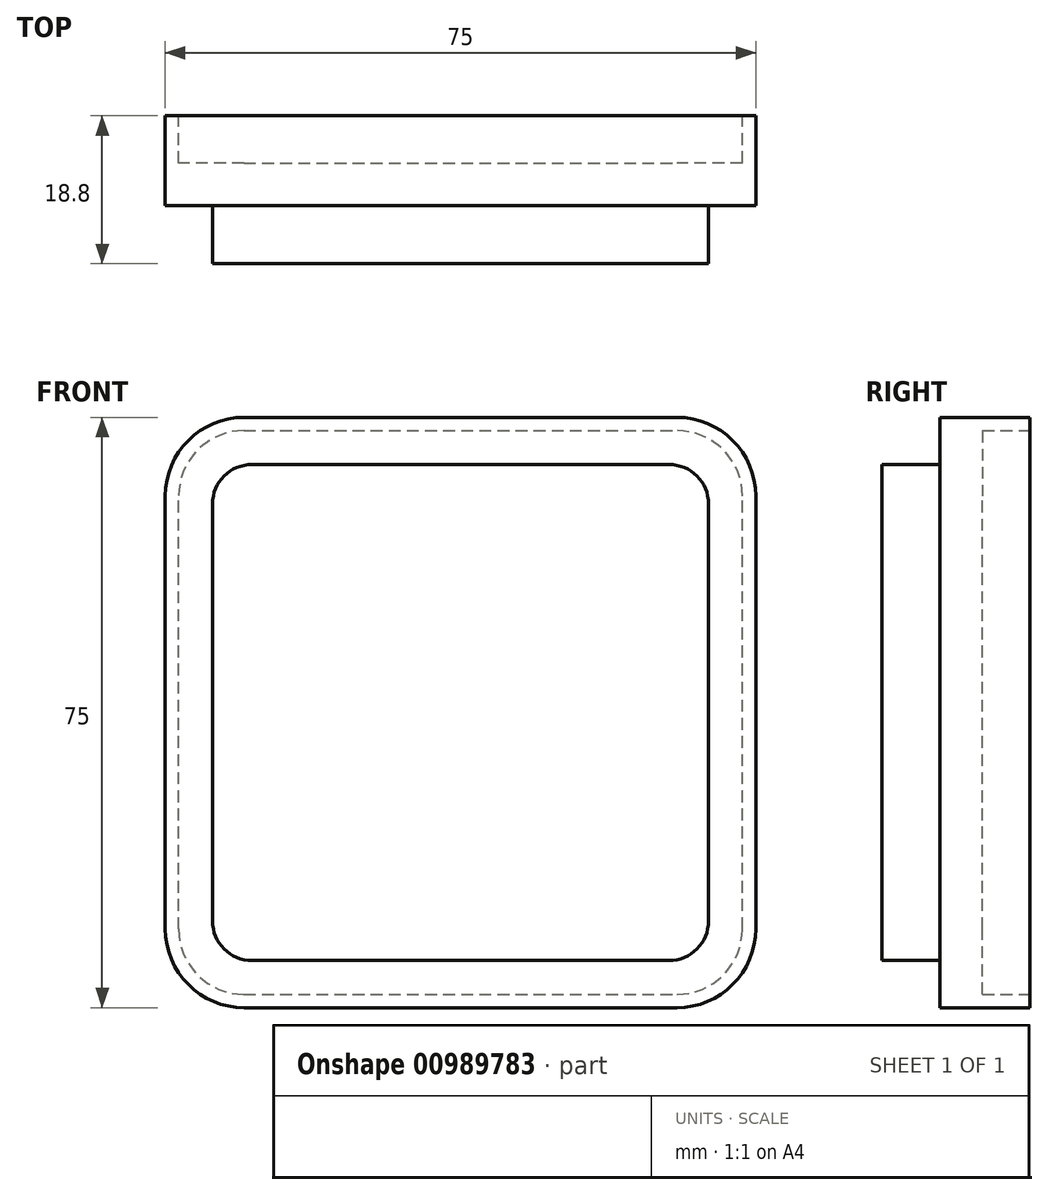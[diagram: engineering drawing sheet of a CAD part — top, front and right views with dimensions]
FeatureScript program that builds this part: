
annotation { "Feature Type Name" : "Feature", "Feature Type Description" : "" }
export const myFeature = defineFeature(function(context is Context, id is Id, definition is map)
    precondition{}
    {
        {
            var Q0;
            Q0=qCreatedBy(makeId("Front.planeOp"),FACE);
            var sketch = newSketch(context, id + "F0", { "sketchPlane" : qUnion([Q0])});
            skLineSegment(sketch, "E0.bottom", {"start": v(10, 0) * mm, "end": v(65, 0) * mm});
            skLineSegment(sketch, "E0.top", {"start": v(10, 75) * mm, "end": v(65, 75) * mm});
            skLineSegment(sketch, "E0.left", {"start": v(0, 10) * mm, "end": v(0, 65) * mm});
            skLineSegment(sketch, "E0.right", {"start": v(75, 10) * mm, "end": v(75, 65) * mm});
            skPoint(sketch, "E1.visualSharp", {"position": v(0, 75) * mm});
            skArc(sketch, "E1.filletArc", {"start": v(10, 75) * mm, "mid": v(2.93, 72.07) * mm, "end": v(0, 65) * mm});
            skPoint(sketch, "E2.visualSharp", {"position": v(75, 75) * mm});
            skArc(sketch, "E2.filletArc", {"start": v(75, 65) * mm, "mid": v(72.07, 72.07) * mm, "end": v(65, 75) * mm});
            skPoint(sketch, "E3.visualSharp", {"position": v(75, 0) * mm});
            skArc(sketch, "E3.filletArc", {"start": v(65, 0) * mm, "mid": v(72.07, 2.93) * mm, "end": v(75, 10) * mm});
            skPoint(sketch, "E4.visualSharp", {"position": v(0, 0) * mm});
            skArc(sketch, "E4.filletArc", {"start": v(0, 10) * mm, "mid": v(2.93, 2.93) * mm, "end": v(10, 0) * mm});
            skArc(sketch, "E5.0", {"start": v(10, 73.3) * mm, "mid": v(4.13, 70.87) * mm, "end": v(1.7, 65) * mm});
            skLineSegment(sketch, "E5.1", {"start": v(1.7, 10) * mm, "end": v(1.7, 65) * mm});
            skLineSegment(sketch, "E5.2", {"start": v(10, 73.3) * mm, "end": v(65, 73.3) * mm});
            skArc(sketch, "E5.3", {"start": v(1.7, 10) * mm, "mid": v(4.13, 4.13) * mm, "end": v(10, 1.7) * mm});
            skArc(sketch, "E5.4", {"start": v(73.3, 65) * mm, "mid": v(70.87, 70.87) * mm, "end": v(65, 73.3) * mm});
            skLineSegment(sketch, "E5.5", {"start": v(73.3, 10) * mm, "end": v(73.3, 65) * mm});
            skArc(sketch, "E5.6", {"start": v(65, 1.7) * mm, "mid": v(70.87, 4.13) * mm, "end": v(73.3, 10) * mm});
            skLineSegment(sketch, "E5.7", {"start": v(10, 1.7) * mm, "end": v(65, 1.7) * mm});
            skSolve(sketch);
        }
        {
            var Q0;
            Q0=makeQuery(id+"F0.imprint","IMPRINT",FACE,{"disambiguationData":[TD([[makeQuery(id+"F0.imprint","IMPRINT",EDGE,{"derivedFrom":sQuery(id+"F0.wireOp",EDGE,"E0.bottom")}),1.0]])]});
            extrude(context, id + "F1", {"entities" : qUnion([Q0]), "depth" : 11.4 * mm, "offsetDistance" : 25 * mm});
        }
        {
            var Q0;
            Q0=makeQuery(id+"F1.opExtrude","CAP_FACE",FACE,{"disambiguationData":[OSD([sQuery(id+"F0.wireOp",EDGE,"E0.bottom"),sQuery(id+"F0.wireOp",EDGE,"E0.top"),sQuery(id+"F0.wireOp",EDGE,"E0.left"),sQuery(id+"F0.wireOp",EDGE,"E0.right"),sQuery(id+"F0.wireOp",EDGE,"E1.filletArc"),sQuery(id+"F0.wireOp",EDGE,"E2.filletArc"),sQuery(id+"F0.wireOp",EDGE,"E3.filletArc"),sQuery(id+"F0.wireOp",EDGE,"E4.filletArc"),sQuery(id+"F0.wireOp",EDGE,"E5.0"),sQuery(id+"F0.wireOp",EDGE,"E5.1"),sQuery(id+"F0.wireOp",EDGE,"E5.2"),sQuery(id+"F0.wireOp",EDGE,"E5.3"),sQuery(id+"F0.wireOp",EDGE,"E5.4"),sQuery(id+"F0.wireOp",EDGE,"E5.5"),sQuery(id+"F0.wireOp",EDGE,"E5.6"),sQuery(id+"F0.wireOp",EDGE,"E5.7")])],"isStart":false});
            var sketch = newSketch(context, id + "F2", { "sketchPlane" : qUnion([Q0])});
            skSolve(sketch);
        }
        {
            var Q0;
            Q0=makeQuery(id+"F2.imprint","IMPRINT",FACE,{"disambiguationData":[TD([[makeQuery(id+"F2.imprint","IMPRINT",EDGE,{"derivedFrom":makeQuery(id+"F1.opExtrude","CAP_EDGE",EDGE,{"disambiguationData":[OSD([sQuery(id+"F0.wireOp",EDGE,"E5.0")])],"isStart":false})}),1.0]])]});
            extrude(context, id + "F3", {"entities" : qUnion([Q0]), "operationType" : NewBodyOperationType.ADD, "oppositeDirection" : true, "depth" : (11.4 - 6) * mm, "offsetDistance" : 25 * mm});
        }
        {
            var Q0;
            {var subQ0=sQuery(id+"F0.wireOp",EDGE,"E5.7");var subQ1=sQuery(id+"F0.wireOp",EDGE,"E5.6");var subQ2=sQuery(id+"F0.wireOp",EDGE,"E5.5");var subQ3=sQuery(id+"F0.wireOp",EDGE,"E5.4");var subQ4=sQuery(id+"F0.wireOp",EDGE,"E5.3");var subQ5=sQuery(id+"F0.wireOp",EDGE,"E5.2");var subQ6=sQuery(id+"F0.wireOp",EDGE,"E5.1");var subQ7=sQuery(id+"F0.wireOp",EDGE,"E5.0");Q0=makeQuery(id+"F3.boolean.opBoolean","MERGE",FACE,{"derivedFrom":[makeQuery(id+"F1.opExtrude","CAP_FACE",FACE,{"disambiguationData":[OSD([sQuery(id+"F0.wireOp",EDGE,"E0.bottom"),sQuery(id+"F0.wireOp",EDGE,"E0.top"),sQuery(id+"F0.wireOp",EDGE,"E0.left"),sQuery(id+"F0.wireOp",EDGE,"E0.right"),sQuery(id+"F0.wireOp",EDGE,"E1.filletArc"),sQuery(id+"F0.wireOp",EDGE,"E2.filletArc"),sQuery(id+"F0.wireOp",EDGE,"E3.filletArc"),sQuery(id+"F0.wireOp",EDGE,"E4.filletArc"),subQ7,subQ6,subQ5,subQ4,subQ3,subQ2,subQ1,subQ0])],"isStart":false}),makeQuery(id+"F3.opExtrude","CAP_FACE",FACE,{"disambiguationData":[OSD([subQ7,subQ6,subQ5,subQ4,subQ3,subQ2,subQ1,subQ0])],"isStart":true})]});}
            var sketch = newSketch(context, id + "F4", { "sketchPlane" : qUnion([Q0])});
            skLineSegment(sketch, "E6", {"start": v(0, 37.5) * mm, "end": v(75, 37.5) * mm, "construction": true});
            skLineSegment(sketch, "E7.bottom", {"start": v(11, 69) * mm, "end": v(64, 69) * mm});
            skLineSegment(sketch, "E7.top", {"start": v(11, 6) * mm, "end": v(64, 6) * mm});
            skLineSegment(sketch, "E7.left", {"start": v(6, 64) * mm, "end": v(6, 11) * mm});
            skLineSegment(sketch, "E7.right", {"start": v(69, 64) * mm, "end": v(69, 11) * mm});
            skPoint(sketch, "E7.middle", {"position": v(37.5, 37.5) * mm});
            skPoint(sketch, "E8.visualSharp", {"position": v(6, 69) * mm});
            skArc(sketch, "E8.filletArc", {"start": v(11, 69) * mm, "mid": v(7.46, 67.54) * mm, "end": v(6, 64) * mm});
            skPoint(sketch, "E9.visualSharp", {"position": v(6, 6) * mm});
            skArc(sketch, "E9.filletArc", {"start": v(6, 11) * mm, "mid": v(7.46, 7.46) * mm, "end": v(11, 6) * mm});
            skPoint(sketch, "E10.visualSharp", {"position": v(69, 6) * mm});
            skArc(sketch, "E10.filletArc", {"start": v(64, 6) * mm, "mid": v(67.54, 7.46) * mm, "end": v(69, 11) * mm});
            skPoint(sketch, "E11.visualSharp", {"position": v(69, 69) * mm});
            skArc(sketch, "E11.filletArc", {"start": v(69, 64) * mm, "mid": v(67.54, 67.54) * mm, "end": v(64, 69) * mm});
            skSolve(sketch);
        }
        {
            var Q0;
            Q0=makeQuery(id+"F4.imprint","IMPRINT",FACE,{"disambiguationData":[TD([[makeQuery(id+"F4.imprint","IMPRINT",EDGE,{"derivedFrom":sQuery(id+"F4.wireOp",EDGE,"E7.bottom")}),-1.0]])]});
            extrude(context, id + "F5", {"entities" : qUnion([Q0]), "operationType" : NewBodyOperationType.ADD, "depth" : 7.4 * mm, "offsetDistance" : 25 * mm});
        }
    });
